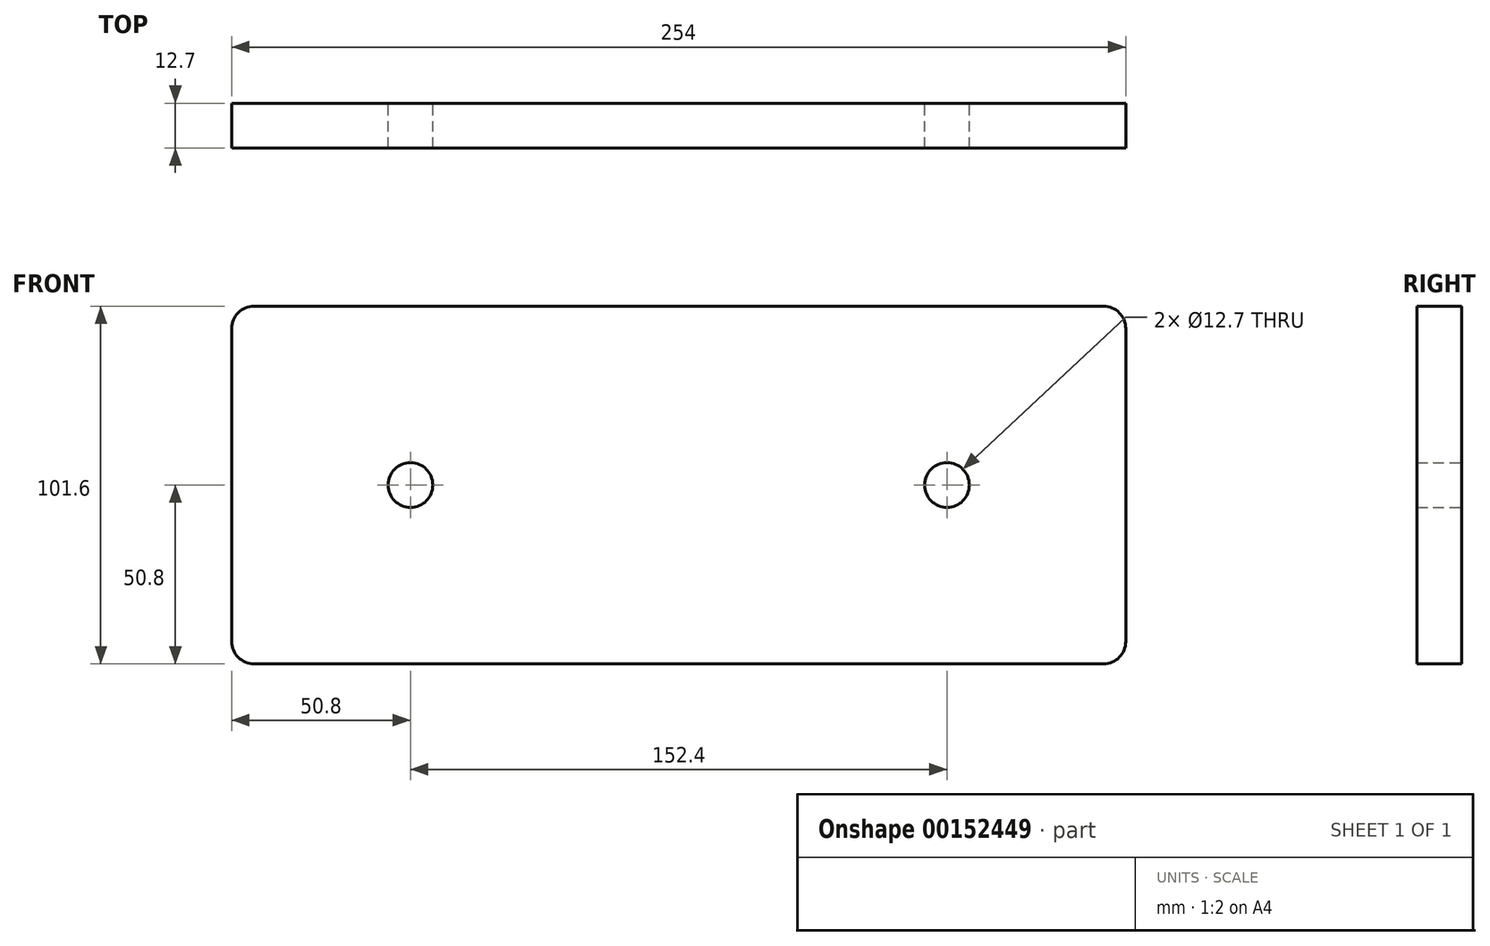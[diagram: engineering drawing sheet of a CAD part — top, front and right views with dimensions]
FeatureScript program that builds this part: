
annotation { "Feature Type Name" : "Feature", "Feature Type Description" : "" }
export const myFeature = defineFeature(function(context is Context, id is Id, definition is map)
    precondition{}
    {
        {
            var Q0;
            Q0=qCreatedBy(makeId("Front.planeOp"),FACE);
            var sketch = newSketch(context, id + "F0", { "sketchPlane" : qUnion([Q0])});
            skLineSegment(sketch, "E0.bottom", {"start": v(0, 0) * mm, "end": v(254, 0) * mm});
            skLineSegment(sketch, "E0.top", {"start": v(0, 101.6) * mm, "end": v(254, 101.6) * mm});
            skLineSegment(sketch, "E0.left", {"start": v(0, 0) * mm, "end": v(0, 101.6) * mm});
            skLineSegment(sketch, "E0.right", {"start": v(254, 0) * mm, "end": v(254, 101.6) * mm});
            skCircle(sketch, "E1", {"center": v(50.8, 50.8) * mm, "radius": 6.35 * mm});
            skPoint(sketch, "E1.centerSnap0", {"position": v(0, 50.8) * mm});
            skCircle(sketch, "E2", {"center": v(203.2, 50.8) * mm, "radius": 6.35 * mm});
            skPoint(sketch, "E2.centerSnap0", {"position": v(254, 50.8) * mm});
            skSolve(sketch);
        }
        {
            var Q0;
            Q0=qSketchRegion(id+"F0",true);
            extrude(context, id + "F1", {"entities" : qUnion([Q0]), "depth" : 12.7 * mm});
        }
        {
            var Q0;
            Q0=makeQuery(id+"F1.opExtrude","SWEPT_EDGE",EDGE,{"disambiguationData":[OSD([sQuery(id+"F0.wireOp",EDGE,"E0.top"),sQuery(id+"F0.wireOp",EDGE,"E0.left")])]});
            var Q1;
            Q1=makeQuery(id+"F1.opExtrude","SWEPT_EDGE",EDGE,{"disambiguationData":[OSD([sQuery(id+"F0.wireOp",EDGE,"E0.bottom"),sQuery(id+"F0.wireOp",EDGE,"E0.left")])]});
            var Q2;
            Q2=makeQuery(id+"F1.opExtrude","SWEPT_EDGE",EDGE,{"disambiguationData":[OSD([sQuery(id+"F0.wireOp",EDGE,"E0.top"),sQuery(id+"F0.wireOp",EDGE,"E0.right")])]});
            var Q3;
            Q3=makeQuery(id+"F1.opExtrude","SWEPT_EDGE",EDGE,{"disambiguationData":[OSD([sQuery(id+"F0.wireOp",EDGE,"E0.bottom"),sQuery(id+"F0.wireOp",EDGE,"E0.right")])]});
            fillet(context, id + "F2", {"entities" : qUnion([Q0, Q1, Q2, Q3]), "radius" : 6.35 * mm, "tangentPropagation" : true, "allowEdgeOverflow" : false});
        }
    });
